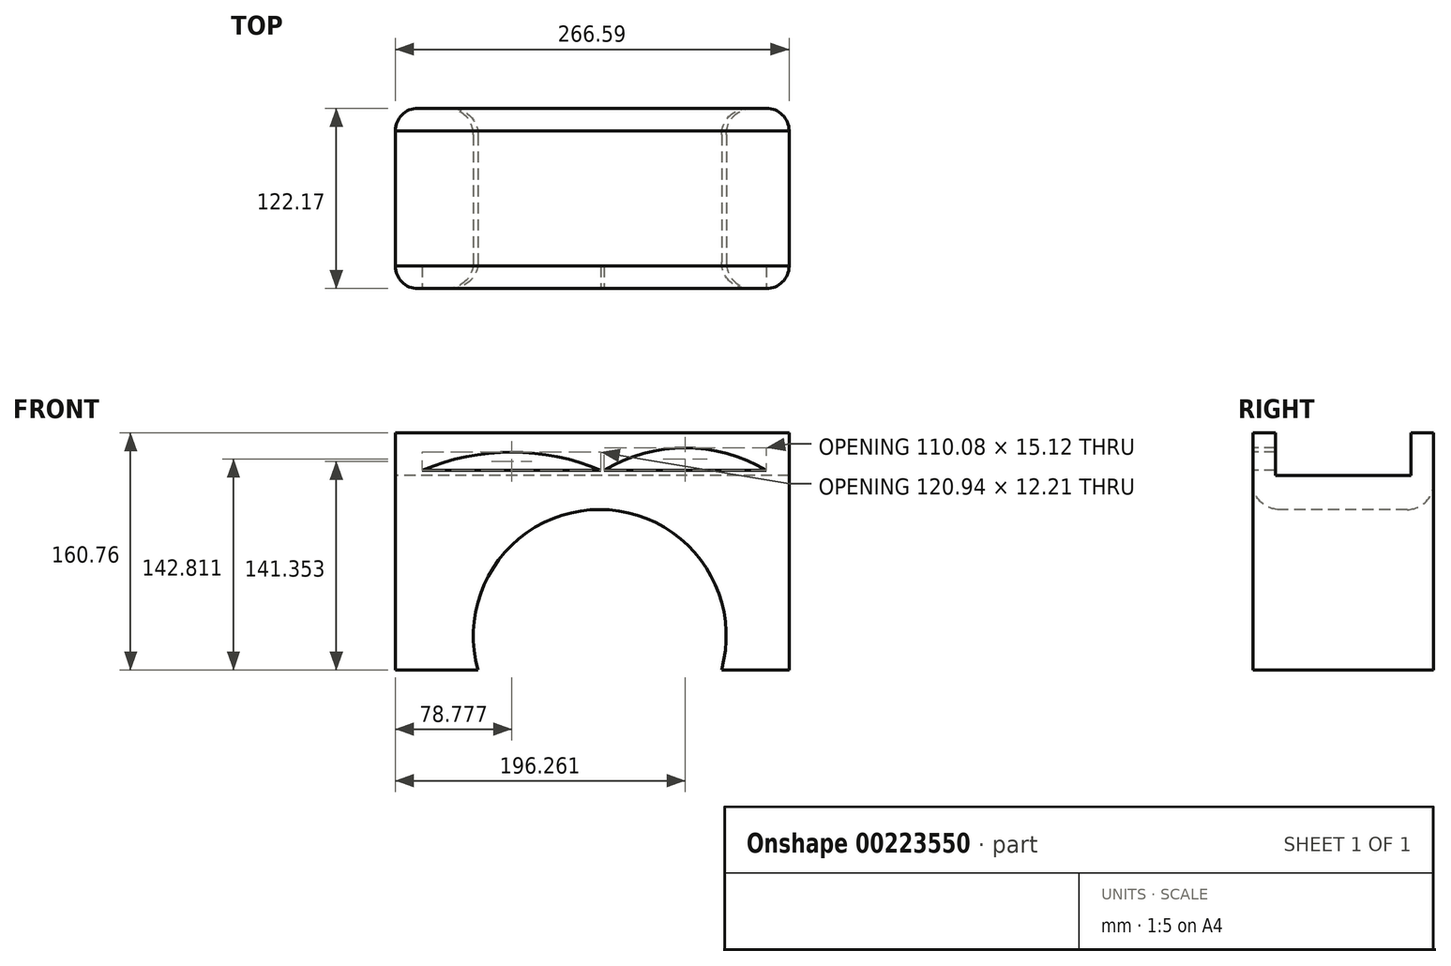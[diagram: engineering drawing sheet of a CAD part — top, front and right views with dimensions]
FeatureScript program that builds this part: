
annotation { "Feature Type Name" : "Feature", "Feature Type Description" : "" }
export const myFeature = defineFeature(function(context is Context, id is Id, definition is map)
    precondition{}
    {
        {
            var Q0;
            Q0=qCreatedBy(makeId("Top.planeOp"),FACE);
            var sketch = newSketch(context, id + "F0", { "sketchPlane" : qUnion([Q0])});
            skLineSegment(sketch, "E0.bottom", {"start": v(70.09, 26.74) * mm, "end": v(-70.09, 26.74) * mm});
            skLineSegment(sketch, "E0.top", {"start": v(70.09, -26.74) * mm, "end": v(-70.09, -26.74) * mm});
            skLineSegment(sketch, "E0.left", {"start": v(70.09, 26.74) * mm, "end": v(70.09, -26.74) * mm});
            skLineSegment(sketch, "E0.right", {"start": v(-70.09, 26.74) * mm, "end": v(-70.09, -26.74) * mm});
            skPoint(sketch, "E0.middle", {"position": v(0, 0) * mm});
            skSolve(sketch);
        }
        {
            var Q0;
            Q0=makeQuery(id+"F0.imprint","IMPRINT",FACE,{"disambiguationData":[TD([[makeQuery(id+"F0.imprint","IMPRINT",EDGE,{"derivedFrom":sQuery(id+"F0.wireOp",EDGE,"E0.bottom")}),1.0]])]});
            extrude(context, id + "F13", {"entities" : qUnion([Q0]), "depth" : 131.88 * mm});
        }
        {
            var Q0;
            Q0=makeQuery(id+"F13.opExtrude","SWEPT_FACE",FACE,{"disambiguationData":[OSD([sQuery(id+"F0.wireOp",EDGE,"E0.right")])]});
            extrude(context, id + "F1", {"entities" : qUnion([Q0]), "operationType" : NewBodyOperationType.ADD, "depth" : 69.77 * mm});
        }
        {
            var Q0;
            Q0=makeQuery(id+"F13.opExtrude","SWEPT_FACE",FACE,{"disambiguationData":[OSD([sQuery(id+"F0.wireOp",EDGE,"E0.left")])]});
            extrude(context, id + "F2", {"entities" : qUnion([Q0]), "operationType" : NewBodyOperationType.ADD, "depth" : 56.64 * mm});
        }
        {
            var Q0;
            {var subQ0=sQuery(id+"F0.wireOp",EDGE,"E0.top");Q0=makeQuery(id+"F2.boolean.opBoolean","MERGE",FACE,{"derivedFrom":[makeQuery(id+"F1.boolean.opBoolean","MERGE",FACE,{"derivedFrom":[makeQuery(id+"F13.opExtrude","SWEPT_FACE",FACE,{"disambiguationData":[OSD([subQ0])]}),makeQuery(id+"F1.opExtrude","SWEPT_FACE",FACE,{"disambiguationData":[OSD([subQ0,sQuery(id+"F0.wireOp",EDGE,"E0.right")])]})]}),makeQuery(id+"F2.opExtrude","SWEPT_FACE",FACE,{"disambiguationData":[OSD([subQ0,sQuery(id+"F0.wireOp",EDGE,"E0.left")])]})]});}
            var sketch = newSketch(context, id + "F3", { "sketchPlane" : qUnion([Q0])});
            skArc(sketch, "E1", {"start": v(81.02, 0) * mm, "mid": v(-1.46, 108.67) * mm, "end": v(-83.93, 0) * mm});
            skSolve(sketch);
        }
        {
            var Q0;
            {var subQ0=sQuery(id+"F3.wireOp",EDGE,"E1");Q0=makeQuery(id+"F3.imprint","IMPRINT",FACE,{"disambiguationData":[TD([[makeQuery(id+"F3.imprint","IMPRINT",EDGE,{"derivedFrom":subQ0}),1.0]])]});}
            extrude(context, id + "F14", {"entities" : qUnion([Q0]), "operationType" : NewBodyOperationType.REMOVE, "oppositeDirection" : true, "depth" : 101.1 * mm});
        }
        {
            var Q0;
            {var subQ0=sQuery(id+"F0.wireOp",EDGE,"E0.top");Q0=makeQuery(id+"F2.boolean.opBoolean","MERGE",FACE,{"derivedFrom":[makeQuery(id+"F1.boolean.opBoolean","MERGE",FACE,{"derivedFrom":[makeQuery(id+"F13.opExtrude","SWEPT_FACE",FACE,{"disambiguationData":[OSD([subQ0])]}),makeQuery(id+"F1.opExtrude","SWEPT_FACE",FACE,{"disambiguationData":[OSD([subQ0,sQuery(id+"F0.wireOp",EDGE,"E0.right")])]})]}),makeQuery(id+"F2.opExtrude","SWEPT_FACE",FACE,{"disambiguationData":[OSD([subQ0,sQuery(id+"F0.wireOp",EDGE,"E0.left")])]})]});}
            extrude(context, id + "F15", {"entities" : qUnion([Q0]), "operationType" : NewBodyOperationType.ADD, "depth" : 68.69 * mm});
        }
        {
            var Q0;
            {var subQ0=sQuery(id+"F0.wireOp",EDGE,"E0.bottom");Q0=makeQuery(id+"F14.boolean.opBoolean","INTERSECT",EDGE,{"derivedFrom":[makeQuery(id+"F2.boolean.opBoolean","MERGE",FACE,{"derivedFrom":[makeQuery(id+"F1.boolean.opBoolean","MERGE",FACE,{"derivedFrom":[makeQuery(id+"F13.opExtrude","SWEPT_FACE",FACE,{"disambiguationData":[OSD([subQ0])]}),makeQuery(id+"F1.opExtrude","SWEPT_FACE",FACE,{"disambiguationData":[OSD([subQ0,sQuery(id+"F0.wireOp",EDGE,"E0.right")])]})]}),makeQuery(id+"F2.opExtrude","SWEPT_FACE",FACE,{"disambiguationData":[OSD([subQ0,sQuery(id+"F0.wireOp",EDGE,"E0.left")])]})]}),makeQuery(id+"F14.opExtrude","SWEPT_FACE",FACE,{"disambiguationData":[OSD([sQuery(id+"F3.wireOp",EDGE,"E1")])]})]});}
            var Q1;
            Q1=makeQuery(id+"F15.opExtrude","CAP_EDGE",EDGE,{"disambiguationData":[OSD([sQuery(id+"F3.wireOp",EDGE,"E1")])],"isStart":false});
            fillet(context, id + "F4", {"entities" : qUnion([Q0, Q1]), "radius" : 17.78 * mm, "tangentPropagation" : true, "allowEdgeOverflow" : false});
        }
        {
            var Q0;
            Q0=makeQuery(id+"F15.opExtrude","CAP_EDGE",EDGE,{"disambiguationData":[OSD([sQuery(id+"F0.wireOp",EDGE,"E0.top"),sQuery(id+"F0.wireOp",EDGE,"E0.left")])],"isStart":false});
            var Q1;
            Q1=makeQuery(id+"F2.opExtrude","CAP_EDGE",EDGE,{"disambiguationData":[OSD([sQuery(id+"F0.wireOp",EDGE,"E0.bottom"),sQuery(id+"F0.wireOp",EDGE,"E0.left")])],"isStart":false});
            var Q2;
            Q2=makeQuery(id+"F15.opExtrude","CAP_EDGE",EDGE,{"disambiguationData":[OSD([sQuery(id+"F0.wireOp",EDGE,"E0.top"),sQuery(id+"F0.wireOp",EDGE,"E0.right")])],"isStart":false});
            var Q3;
            Q3=makeQuery(id+"F1.opExtrude","CAP_EDGE",EDGE,{"disambiguationData":[OSD([sQuery(id+"F0.wireOp",EDGE,"E0.bottom"),sQuery(id+"F0.wireOp",EDGE,"E0.right")])],"isStart":false});
            fillet(context, id + "F5", {"entities" : qUnion([Q0, Q1, Q2, Q3]), "radius" : 15.24 * mm, "tangentPropagation" : true, "allowEdgeOverflow" : false});
        }
        {
            var Q0;
            {var subQ0=sQuery(id+"F0.wireOp",EDGE,"E0.left");var subQ1=sQuery(id+"F0.wireOp",EDGE,"E0.top");var subQ2=sQuery(id+"F0.wireOp",EDGE,"E0.right");Q0=makeQuery(id+"F15.boolean.opBoolean","MERGE",FACE,{"derivedFrom":[makeQuery(id+"F2.boolean.opBoolean","MERGE",FACE,{"derivedFrom":[makeQuery(id+"F1.boolean.opBoolean","MERGE",FACE,{"derivedFrom":[makeQuery(id+"F13.opExtrude","CAP_FACE",FACE,{"disambiguationData":[OSD([sQuery(id+"F0.wireOp",EDGE,"E0.bottom"),subQ1,subQ0,subQ2])],"isStart":false}),makeQuery(id+"F1.opExtrude","SWEPT_FACE",FACE,{"disambiguationData":[OSD([subQ2]),TDD([makeQuery(id+"F13.opExtrude","CAP_EDGE",EDGE,{"disambiguationData":[OSD([subQ2])],"isStart":false})])]})]}),makeQuery(id+"F2.opExtrude","SWEPT_FACE",FACE,{"disambiguationData":[OSD([subQ0]),TDD([makeQuery(id+"F13.opExtrude","CAP_EDGE",EDGE,{"disambiguationData":[OSD([subQ0])],"isStart":false})])]})]}),makeQuery(id+"F15.opExtrude","SWEPT_FACE",FACE,{"disambiguationData":[OSD([subQ1,subQ0,subQ2]),TDD([makeQuery(id+"F2.boolean.opBoolean","MERGE",EDGE,{"derivedFrom":[makeQuery(id+"F1.boolean.opBoolean","MERGE",EDGE,{"derivedFrom":[makeQuery(id+"F13.opExtrude","CAP_EDGE",EDGE,{"disambiguationData":[OSD([subQ1])],"isStart":false}),makeQuery(id+"F1.opExtrude","SWEPT_EDGE",EDGE,{"disambiguationData":[OSD([subQ1,subQ2]),TDD([makeQuery(id+"F13.opExtrude","CAP_VERTEX",VERTEX,{"disambiguationData":[OSD([subQ1,subQ2])],"isStart":false})])]})]}),makeQuery(id+"F2.opExtrude","SWEPT_EDGE",EDGE,{"disambiguationData":[OSD([subQ1,subQ0]),TDD([makeQuery(id+"F13.opExtrude","CAP_VERTEX",VERTEX,{"disambiguationData":[OSD([subQ1,subQ0])],"isStart":false})])]})]})])]})]});}
            var sketch = newSketch(context, id + "F16", { "sketchPlane" : qUnion([Q0])});
            skLineSegment(sketch, "E2.bottom", {"start": v(126.73, -80.2) * mm, "end": v(-139.86, -80.2) * mm});
            skLineSegment(sketch, "E2.top", {"start": v(126.73, 11.5) * mm, "end": v(-139.86, 11.5) * mm});
            skLineSegment(sketch, "E2.left", {"start": v(126.73, -80.2) * mm, "end": v(126.73, 11.5) * mm});
            skLineSegment(sketch, "E2.right", {"start": v(-139.86, -80.2) * mm, "end": v(-139.86, 11.5) * mm});
            skSolve(sketch);
        }
        {
            var Q0;
            Q0=makeQuery(id+"F16.imprint","IMPRINT",FACE,{"disambiguationData":[TD([[makeQuery(id+"F16.imprint","IMPRINT",EDGE,{"derivedFrom":sQuery(id+"F16.wireOp",EDGE,"E2.bottom")}),1.0]])]});
            var Q1;
            Q1=makeQuery(id+"F16.imprint","IMPRINT",FACE,{"disambiguationData":[TD([[makeQuery(id+"F16.imprint","IMPRINT",EDGE,{"derivedFrom":sQuery(id+"F16.wireOp",EDGE,"E2.top")}),-1.0]])]});
            extrude(context, id + "F6", {"entities" : qUnion([Q0, Q1]), "operationType" : NewBodyOperationType.ADD, "depth" : 28.88 * mm});
        }
        {
            var Q0;
            {var subQ0=sQuery(id+"F0.wireOp",EDGE,"E0.right");var subQ1=sQuery(id+"F0.wireOp",EDGE,"E0.left");var subQ2=sQuery(id+"F0.wireOp",EDGE,"E0.top");Q0=makeQuery(id+"F6.boolean.opBoolean","MERGE",FACE,{"derivedFrom":[makeQuery(id+"F15.opExtrude","CAP_FACE",FACE,{"disambiguationData":[OSD([subQ2,subQ1,subQ0])],"isStart":false}),makeQuery(id+"F6.opExtrude","SWEPT_FACE",FACE,{"disambiguationData":[OSD([subQ2,subQ1,subQ0])]})]});}
            var sketch = newSketch(context, id + "F7", { "sketchPlane" : qUnion([Q0])});
            skLineSegment(sketch, "E3", {"start": v(-124.62, 135.25) * mm, "end": v(-39.34, 135.25) * mm});
            skLineSegment(sketch, "E4", {"start": v(-39.34, 135.25) * mm, "end": v(9.94, 135.25) * mm});
            skLineSegment(sketch, "E5", {"start": v(9.94, 135.25) * mm, "end": v(111.49, 135.25) * mm});
            skSolve(sketch);
        }
        {
            var Q0;
            {var subQ5=sQuery(id+"F7.wireOp",EDGE,"E3");Q0=makeQuery(id+"F7.imprint","IMPRINT",FACE,{"disambiguationData":[TD([[makeQuery(id+"F7.imprint","IMPRINT",EDGE,{"derivedFrom":subQ5}),1.0]])]});}
            var sketch = newSketch(context, id + "F8", { "sketchPlane" : qUnion([Q0])});
            skLineSegment(sketch, "E6", {"start": v(0, 161) * mm, "end": v(0, 135.18) * mm});
            skSolve(sketch);
        }
        {
            var Q0;
            {var subQ5=sQuery(id+"F7.wireOp",EDGE,"E3");Q0=makeQuery(id+"F7.imprint","IMPRINT",FACE,{"disambiguationData":[TD([[makeQuery(id+"F7.imprint","IMPRINT",EDGE,{"derivedFrom":subQ5}),1.0]])]});}
            var sketch = newSketch(context, id + "F9", { "sketchPlane" : qUnion([Q0])});
            skArc(sketch, "E7", {"start": v(0, 135) * mm, "mid": v(-61.76, 147.45) * mm, "end": v(-123.42, 134.45) * mm});
            skSolve(sketch);
        }
        {
            var Q0;
            {var subQ0=sQuery(id+"F9.wireOp",EDGE,"E7");var subQ1=makeQuery(id+"F7.imprint","IMPRINT",EDGE,{"derivedFrom":sQuery(id+"F7.wireOp",EDGE,"E3")});var subQ2=makeQuery(id+"F9.imprint","INTERSECT",VERTEX,{"derivedFrom":[subQ1,subQ0]});Q0=makeQuery(id+"F9.imprint","IMPRINT",FACE,{"disambiguationData":[TD([[makeQuery(id+"F9.imprint","IMPRINT",EDGE,{"disambiguationData":[TD([[subQ2,1.0]])],"derivedFrom":subQ0}),1.0]])]});}
            extrude(context, id + "F10", {"entities" : qUnion([Q0]), "operationType" : NewBodyOperationType.REMOVE, "oppositeDirection" : true, "depth" : 25.4 * mm});
        }
        {
            var Q0;
            {var subQ0=sQuery(id+"F7.wireOp",EDGE,"E5");var subQ1=makeQuery(id+"F7.imprint","IMPRINT",EDGE,{"derivedFrom":subQ0});Q0=makeQuery(id+"F8.imprint","IMPRINT",FACE,{"disambiguationData":[TD([[makeQuery(id+"F8.imprint","IMPRINT",EDGE,{"derivedFrom":subQ1}),1.0]])]});}
            var sketch = newSketch(context, id + "F11", { "sketchPlane" : qUnion([Q0])});
            skArc(sketch, "E8", {"start": v(111.78, 135.04) * mm, "mid": v(55.8, 150.37) * mm, "end": v(0, 134.43) * mm});
            skSolve(sketch);
        }
        {
            var Q0;
            {var subQ0=sQuery(id+"F11.wireOp",EDGE,"E8");var subQ1=makeQuery(id+"F7.imprint","IMPRINT",EDGE,{"derivedFrom":sQuery(id+"F7.wireOp",EDGE,"E5")});var subQ2=makeQuery(id+"F8.imprint","IMPRINT",EDGE,{"derivedFrom":subQ1});var subQ3=makeQuery(id+"F11.imprint","INTERSECT",VERTEX,{"derivedFrom":[subQ2,subQ0]});Q0=makeQuery(id+"F11.imprint","IMPRINT",FACE,{"disambiguationData":[TD([[makeQuery(id+"F11.imprint","IMPRINT",EDGE,{"disambiguationData":[TD([[subQ3,-1.0]])],"derivedFrom":subQ0}),1.0]])]});}
            extrude(context, id + "F12", {"entities" : qUnion([Q0]), "operationType" : NewBodyOperationType.REMOVE, "oppositeDirection" : true, "depth" : 25.4 * mm});
        }
    });
